# Revit family: EKF_EE_РейкаПоперечнаяUNIT_PROxima
name_source: partatom
category: Электрооборудование
units: mm (PartAtom-declared; Revit-internal decimal feet)

## family parameters
Всегда вертикально = Нет
На основе рабочей плоскости = Да
Общий = Да
При загрузке вырезать с полостями = Нет
Размер круглого соединителя = Использовать диаметр
Тип детали = Силовой щит
Точка расчета площади = Нет

## types (2) — shared parameters
ADSK_Единица измерения = шт.
ADSK_Завод-изготовитель = EKF
ADSK_Количество = 1
ADSK_Марка = Рейка поперечная
ADSK_Материал = Сталь_Оцинкованная
ADSK_Обозначение = Рейка поперечная
ADSK_Размер_Высота = 50 мм
ADSK_Размер_Глубина = 10 мм
b = 35 мм
t = 1.2 мм
Изготовитель = EKF
Серия номенклатуры = Unit PROxima
Степень защиты IP = -
ТВ = EKF_2
Тип установки = -
Фаска = 10 мм
Шаг = 20 мм
zero-valued in all types: ADSK_Масса, Отметка по умолчанию

## per-type parameters (varying)
| type | ADSK_Код изделия | ADSK_Размер_Ширина | Отступ | Тип |
| Рейка поперечная для ВРУ Unit глубиной 450мм EKF PROxima | mb-15-rp-45 | 310 мм | 15 мм | 75 мм |
| Рейка поперечная для ВРУ Unit глубиной 600мм EKF PROxima | mb-15-rp-60 | 460 мм | 20 мм | 76 мм |

note: column(s) folded — value = type name in every type: ADSK_Наименование
